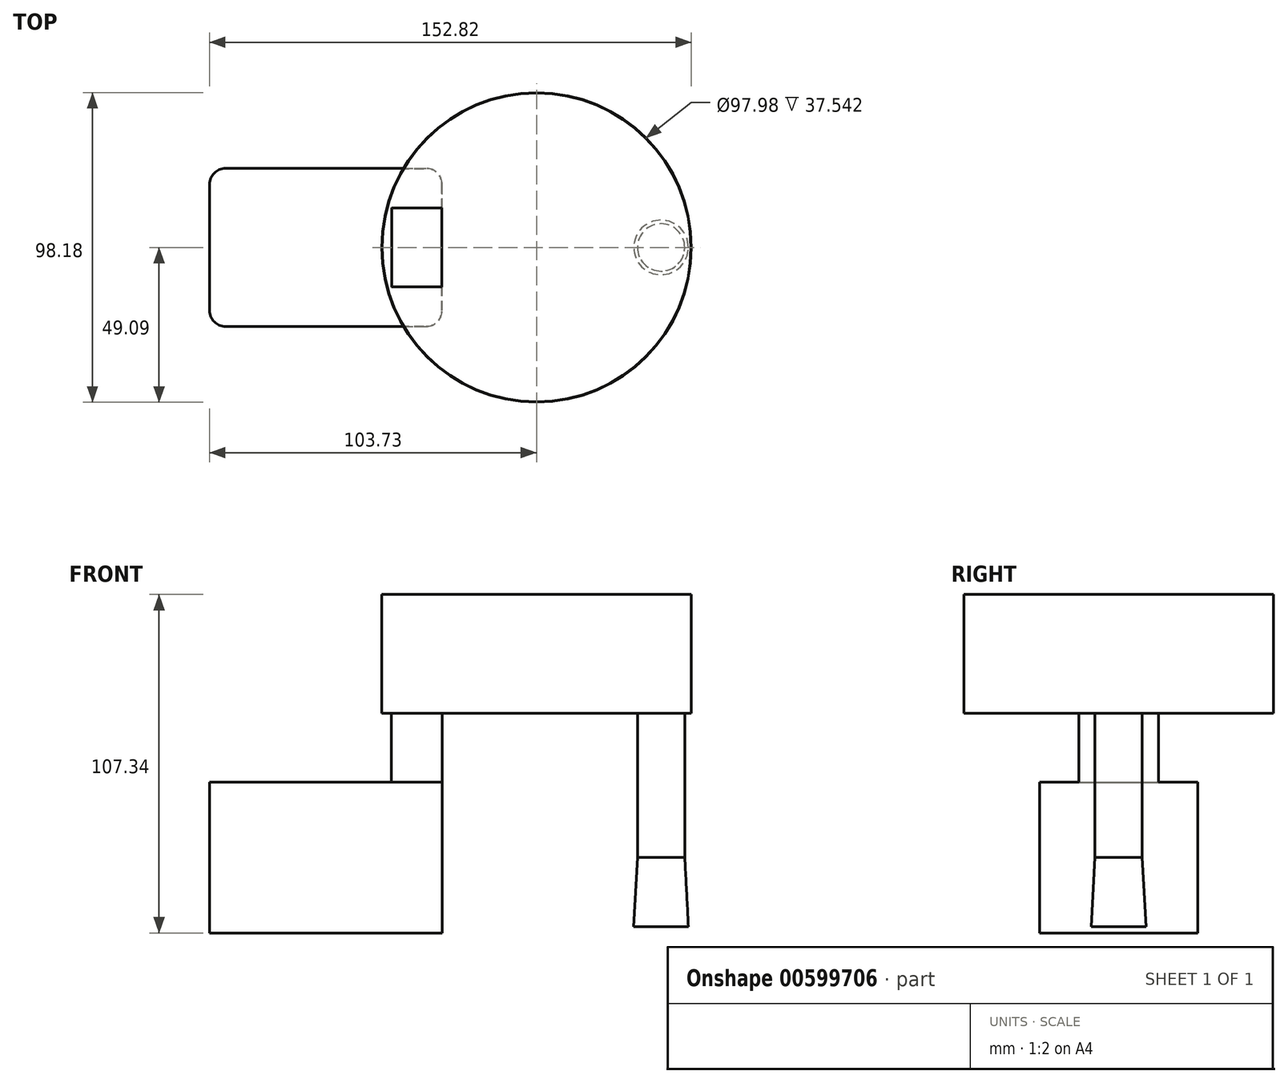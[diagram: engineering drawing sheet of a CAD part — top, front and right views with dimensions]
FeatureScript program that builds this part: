
annotation { "Feature Type Name" : "Feature", "Feature Type Description" : "" }
export const myFeature = defineFeature(function(context is Context, id is Id, definition is map)
    precondition{}
    {
        {
            var Q0;
            Q0=qCreatedBy(makeId("Front.planeOp"),FACE);
            var sketch = newSketch(context, id + "F0", { "sketchPlane" : qUnion([Q0])});
            skLineSegment(sketch, "E0.bottom", {"start": v(-36.82, -23.8) * mm, "end": v(36.82, -23.8) * mm});
            skLineSegment(sketch, "E0.top", {"start": v(-36.82, 23.8) * mm, "end": v(36.82, 23.8) * mm});
            skLineSegment(sketch, "E0.left", {"start": v(-36.82, -23.8) * mm, "end": v(-36.82, 23.8) * mm});
            skLineSegment(sketch, "E0.right", {"start": v(36.82, -23.8) * mm, "end": v(36.82, 23.8) * mm});
            skPoint(sketch, "E0.middle", {"position": v(0, 0) * mm});
            skLineSegment(sketch, "E1", {"start": v(36.82, 23.8) * mm, "end": v(36.82, 49.5) * mm});
            skArc(sketch, "E2", {"start": v(36.82, 49.5) * mm, "mid": v(41.26, 60.22) * mm, "end": v(51.98, 64.66) * mm});
            skLineSegment(sketch, "E3", {"start": v(51.98, 64.66) * mm, "end": v(91.25, 64.66) * mm});
            skLineSegment(sketch, "E4.bottom", {"start": v(66.8, 45.89) * mm, "end": v(115.8, 45.89) * mm});
            skLineSegment(sketch, "E4.top", {"start": v(66.8, 83.43) * mm, "end": v(115.8, 83.43) * mm});
            skLineSegment(sketch, "E4.left", {"start": v(66.8, 45.89) * mm, "end": v(66.8, 83.43) * mm});
            skLineSegment(sketch, "E4.right", {"start": v(115.8, 45.89) * mm, "end": v(115.8, 83.43) * mm});
            skPoint(sketch, "E4.middle", {"position": v(91.3, 64.66) * mm});
            skLineSegment(sketch, "E5.0", {"start": v(51.98, 80.66) * mm, "end": v(91.25, 80.66) * mm});
            skArc(sketch, "E5.1", {"start": v(20.82, 49.5) * mm, "mid": v(29.94, 71.54) * mm, "end": v(51.98, 80.66) * mm});
            skLineSegment(sketch, "E5.2", {"start": v(20.82, 23.8) * mm, "end": v(20.82, 49.5) * mm});
            skSolve(sketch);
        }
        {
            var Q0;
            Q0=makeQuery(id+"F0.imprint","IMPRINT",FACE,{"disambiguationData":[TD([[makeQuery(id+"F0.imprint","IMPRINT",EDGE,{"derivedFrom":sQuery(id+"F0.wireOp",EDGE,"E0.bottom")}),1.0]])]});
            extrude(context, id + "F1", {"entities" : qUnion([Q0]), "endBound" : BoundingType.SYMMETRIC, "depth" : 50 * mm, "offsetDistance" : 25 * mm});
        }
        {
            var Q0;
            {var subQ1=sQuery(id+"F0.wireOp",EDGE,"E1");Q0=makeQuery(id+"F0.imprint","IMPRINT",FACE,{"disambiguationData":[TD([[makeQuery(id+"F0.imprint","IMPRINT",EDGE,{"derivedFrom":subQ1}),1.0]])]});}
            extrude(context, id + "F2", {"entities" : qUnion([Q0]), "operationType" : NewBodyOperationType.ADD, "endBound" : BoundingType.SYMMETRIC, "depth" : 25 * mm, "offsetDistance" : 25 * mm});
        }
        {
            var Q0;
            {var subQ3=sQuery(id+"F0.wireOp",EDGE,"E4.bottom");Q0=makeQuery(id+"F0.imprint","IMPRINT",FACE,{"disambiguationData":[TD([[makeQuery(id+"F0.imprint","IMPRINT",EDGE,{"derivedFrom":subQ3}),1.0]])]});}
            var Q1;
            Q1=sQuery(id+"F0.wireOp",EDGE,"E4.left");
            revolve(context, id + "F3", {"operationType" : NewBodyOperationType.ADD, "entities" : qUnion([Q0]), "axis" : qUnion([Q1]), "revolveType" : RevolveType.FULL});
        }
        {
            var Q0;
            Q0=makeQuery(id+"F1.opExtrude","CAP_EDGE",EDGE,{"disambiguationData":[OSD([sQuery(id+"F0.wireOp",EDGE,"E0.right")])],"isStart":false});
            var Q1;
            Q1=makeQuery(id+"F1.opExtrude","CAP_EDGE",EDGE,{"disambiguationData":[OSD([sQuery(id+"F0.wireOp",EDGE,"E0.left")])],"isStart":false});
            var Q2;
            Q2=makeQuery(id+"F1.opExtrude","CAP_EDGE",EDGE,{"disambiguationData":[OSD([sQuery(id+"F0.wireOp",EDGE,"E0.right")])],"isStart":true});
            var Q3;
            Q3=makeQuery(id+"F1.opExtrude","CAP_EDGE",EDGE,{"disambiguationData":[OSD([sQuery(id+"F0.wireOp",EDGE,"E0.left")])],"isStart":true});
            fillet(context, id + "F4", {"entities" : qUnion([Q0, Q1, Q2, Q3]), "radius" : 5 * mm, "tangentPropagation" : true, "allowEdgeOverflow" : false});
        }
        {
            var Q0;
            Q0=makeQuery(id+"F3.opRevolve","SWEPT_FACE",FACE,{"disambiguationData":[OSD([sQuery(id+"F0.wireOp",EDGE,"E4.top")])]});
            shell(context, id + "F5", {"entities" : qUnion([Q0]), "thickness" : 0.1 * mm, "oppositeDirection" : true});
        }
        {
            var Q0;
            Q0=qCreatedBy(makeId("Top.planeOp"),FACE);
            var sketch = newSketch(context, id + "F6", { "sketchPlane" : qUnion([Q0])});
            skCircle(sketch, "E6", {"center": v(106.3, 0) * mm, "radius": 7.51 * mm});
            skSolve(sketch);
        }
        {
            var Q0;
            Q0 = qSketchRegion(id + "F6", true);
            extrude(context, id + "F7", {"entities" : qUnion([Q0]), "operationType" : NewBodyOperationType.ADD, "endBound" : BoundingType.UP_TO_NEXT, "depth" : 40 * mm, "offsetDistance" : 25 * mm, "hasSecondDirection" : true, "secondDirectionOppositeDirection" : true, "secondDirectionDepth" : 21.9 * mm, "hasSecondDirectionDraft" : true, "secondDirectionDraftAngle" : 3 * degree});
        }
    });
